# Revit family: HUNTER_I-40-06-SS-ON
name_source: partatom
category: Sprinklers
revit_build: Autodesk Revit 2017 (Build: 20160225_1515(x64)
units: mm (PartAtom-declared; Revit-internal decimal feet)

## family parameters
Always vertical = Yes
Cut with Voids When Loaded = No
Maintain Annotation Orientation = No
OmniClass Number = 23.11.27.15.11.11
OmniClass Title = Installed Sprinkler Heads
Part Type = Normal
Room Calculation Point = No
Round Connector Dimension = Use Diameter
Shared = Yes
Work Plane-Based = No

## types (6) — shared parameters
Arc Max = 360.00°
Arc Min = 360.00°
Assembly Code = G2050700
Body Height = 200 mm  [stored 0.656168 ft]
Body Material = Hunter® ABS Plastic
Connection_Dia = 30 mm  [stored 0.0984252 ft]
Diameter = 610 mm
Exposed Diameter = 50 mm  [stored 0.164042 ft]
Inlet Size = 1" BSP
Keynote = 328423.02
Manufacturer = Hunter® Industries
Pop Up Height = 100 mm  [stored 0.328084 ft]
Pop Up Material = Hunter® Stainless Steel
Pressure = 500.0 kPa
Show 2D Symbol = Yes
Show Water Spray = Yes
Trajectory Angle = 25.00°
Type Comments = Rotor I-40-06 with Plastic Riser
Type Image = <None>
URL = https://www.hunterindustries.com
Water = Water
Water Pattern = Water Arc

## per-type parameters (varying)
| type | Description | Model | Nozzle Size | Nozzle Tag | Precipitation Rate | Trajectory Radius |
| I-40-06-SS-ON-B Dual Opposing  15 Grey -5.0bar-17.10m | Hunter I-40-06 Rotor Body with Preinstalled Check in Valve, stainless steel riser and (15 Grey) Dual Opposing Nozzle | I-40-04-SS-ON-B-15 Grey | Hunter® (15 Grey) Dual Opposing Nozzle | I-40-06-SS-ON-B-15Grey | 13 mm/hr | 17100 mm |
| I-40-06-SS-ON-B Dual Opposing 18 Red -5.0bar-18.30m | Hunter I-40-06 Rotor Body with Preinstalled Check in Valve, stainless steel riser and (18 Red) Dual Opposing Nozzle | I-40-04-SS-ON-B-18 Red | Hunter® (18 Red) Dual Opposing Nozzle | I-40-06-SS-ON-B-18Red | 13 mm/hr | 18300 mm |
| I-40-06-SS-ON-B Dual Opposing 20 Dk.brown -5.0bar-19.50m | Hunter I-40-06 Rotor Body with Preinstalled Check in Valve, stainless steel riser and (20 Dk. brown) Dual Opposing Nozzle | I-40-04-SS-ON-B-20 Dk.brown | Hunter® (20 Dk.Brown) Dual Opposing Nozzle | I-40-06-SS-ON-B-20 Dk.brown | 15 mm/hr | 19500 mm |
| I-40-06-SS-ON-B Dual Opposing 23 Dk. Green -5.0bar-20.10m | Hunter I-40-06 Rotor Body with Preinstalled Check in Valve, stainless steel riser and (23 Dk. green) Dual Opposing Nozzle | I-40-04-SS-ON-B-23 Dk.green | Hunter® (23 Dk.Green) Dual Opposing Nozzle | I-40-06-SS-ON-B-23 Dk.green | 15 mm/hr | 20100 mm |
| I-40-06-SS-ON-B Dual Opposing 25 Dk.blue -5.0bar-20.70m | Hunter I-40-06 Rotor Body with Preinstalled Check in Valve, stainless steel riser and (25 Dk. blue) Dual Opposing Nozzle | I-40-04-SS-ON-B-25 Dk.blue | Hunter® (25 Dk.blue) Dual Opposing Nozzle | I-40-06-SS-ON-B-25 Dk.blue | 15 mm/hr | 20700 mm |
| I-40-06-SS-ON-B Dual Opposing 28 Black -5.0bar-21.30m | Hunter I-40-06 Rotor Body with Preinstalled Check in Valve, stainless steel riser and (28 Black) Dual Opposing Nozzle | I-40-04-SS-ON-B-28 Black | Hunter® (25 Dk.blue) Dual Opposing Nozzle | I-40-06-SS-ON-B-28 Black | 15 mm/hr | 21300 mm |

note: [stored X ft] marks values corroborated as IEEE doubles in the binary element streams (Revit-internal decimal feet)

## geometry (parser evidence)
native form markers: Sweep x10
no freeform markers — native parametric forms only
